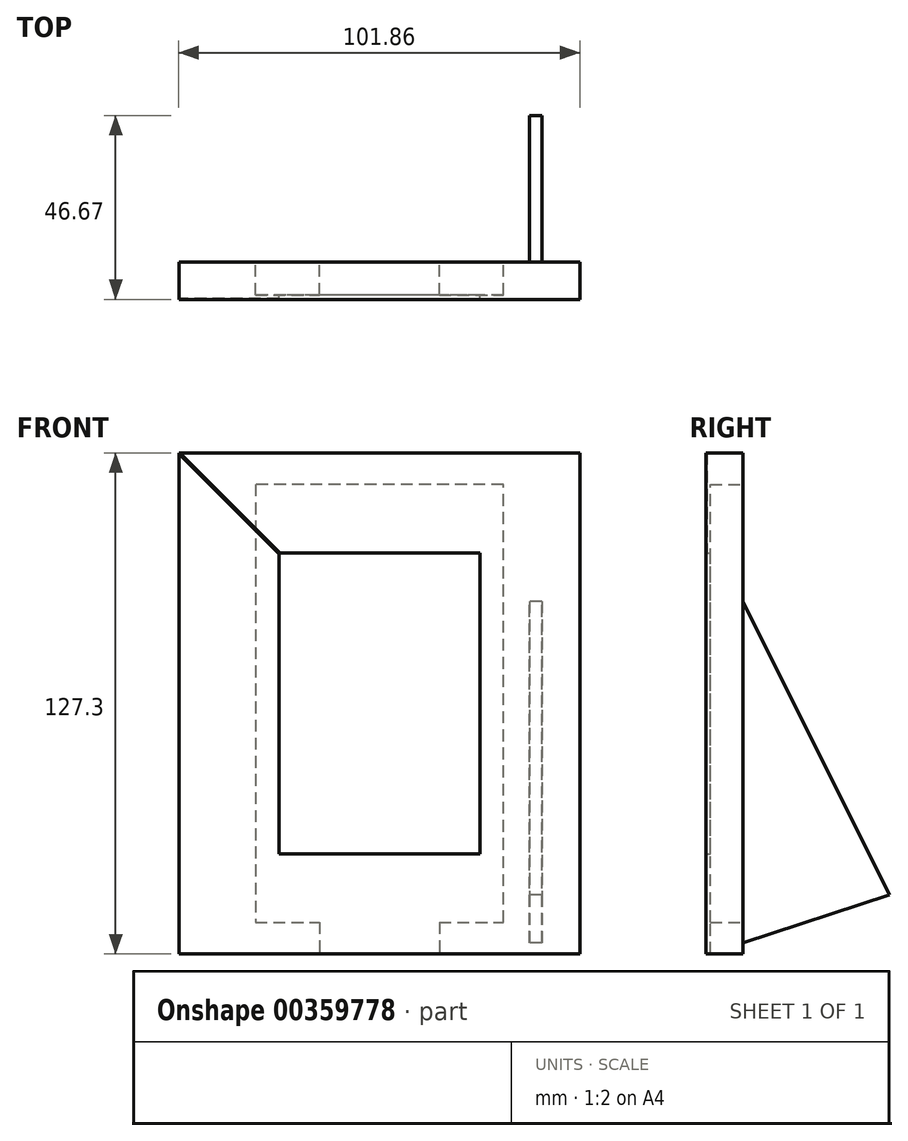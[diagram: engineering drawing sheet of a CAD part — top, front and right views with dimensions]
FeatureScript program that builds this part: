
annotation { "Feature Type Name" : "Feature", "Feature Type Description" : "" }
export const myFeature = defineFeature(function(context is Context, id is Id, definition is map)
    precondition{}
    {
        {
            var Q0;
            Q0=qCreatedBy(makeId("Front.planeOp"),FACE);
            var sketch = newSketch(context, id + "F0", { "sketchPlane" : qUnion([Q0])});
            skLineSegment(sketch, "E0.bottom", {"start": v(-22.23, 55.25) * mm, "end": v(22.23, 55.25) * mm});
            skLineSegment(sketch, "E0.top", {"start": v(-22.23, -55.25) * mm, "end": v(22.23, -55.25) * mm});
            skLineSegment(sketch, "E0.left", {"start": v(-31.12, 46.35) * mm, "end": v(-31.12, -46.36) * mm});
            skLineSegment(sketch, "E0.right", {"start": v(31.12, 46.35) * mm, "end": v(31.12, -46.36) * mm});
            skPoint(sketch, "E1.visualSharp", {"position": v(-31.12, 55.25) * mm});
            skArc(sketch, "E1.filletArc", {"start": v(-22.23, 55.24) * mm, "mid": v(-28.51, 52.64) * mm, "end": v(-31.12, 46.35) * mm});
            skPoint(sketch, "E2.visualSharp", {"position": v(-31.12, -55.25) * mm});
            skArc(sketch, "E2.filletArc", {"start": v(-31.12, -46.36) * mm, "mid": v(-28.51, -52.64) * mm, "end": v(-22.23, -55.25) * mm});
            skPoint(sketch, "E3.visualSharp", {"position": v(31.12, -55.25) * mm});
            skArc(sketch, "E3.filletArc", {"start": v(22.23, -55.25) * mm, "mid": v(28.51, -52.64) * mm, "end": v(31.12, -46.36) * mm});
            skPoint(sketch, "E4.visualSharp", {"position": v(31.12, 55.25) * mm});
            skArc(sketch, "E4.filletArc", {"start": v(31.12, 46.35) * mm, "mid": v(28.51, 52.64) * mm, "end": v(22.23, 55.25) * mm});
            skSolve(sketch);
        }
        {
            var Q0;
            Q0=makeQuery(id+"F0.imprint","IMPRINT",FACE,{"disambiguationData":[TD([[makeQuery(id+"F0.imprint","IMPRINT",EDGE,{"derivedFrom":sQuery(id+"F0.wireOp",EDGE,"E0.bottom")}),-1.0]])]});
            var sketch = newSketch(context, id + "F1", { "sketchPlane" : qUnion([Q0])});
            skLineSegment(sketch, "E5.bottom", {"start": v(-25.53, 38.25) * mm, "end": v(25.53, 38.25) * mm});
            skLineSegment(sketch, "E5.top", {"start": v(-25.53, -38.25) * mm, "end": v(25.53, -38.25) * mm});
            skLineSegment(sketch, "E5.left", {"start": v(-25.53, 38.25) * mm, "end": v(-25.53, -38.25) * mm});
            skLineSegment(sketch, "E5.right", {"start": v(25.53, 38.25) * mm, "end": v(25.53, -38.25) * mm});
            skSolve(sketch);
        }
        {
            var Q0;
            Q0=qCreatedBy(makeId("Front.planeOp"),FACE);
            var sketch = newSketch(context, id + "F2", { "sketchPlane" : qUnion([Q0])});
            skLineSegment(sketch, "E6.bottom", {"start": v(-25.53, 38.25) * mm, "end": v(25.53, 38.25) * mm});
            skLineSegment(sketch, "E6.top", {"start": v(-25.53, -38.25) * mm, "end": v(25.53, -38.25) * mm});
            skLineSegment(sketch, "E6.left", {"start": v(-25.53, 38.25) * mm, "end": v(-25.53, -38.25) * mm});
            skLineSegment(sketch, "E6.right", {"start": v(25.53, 38.25) * mm, "end": v(25.53, -38.25) * mm});
            skLineSegment(sketch, "E7.bottom", {"start": v(-50.93, 63.65) * mm, "end": v(50.93, 63.65) * mm});
            skLineSegment(sketch, "E7.top", {"start": v(-50.93, -63.65) * mm, "end": v(50.93, -63.65) * mm});
            skLineSegment(sketch, "E7.left", {"start": v(-50.93, 63.65) * mm, "end": v(-50.93, -63.65) * mm});
            skLineSegment(sketch, "E7.right", {"start": v(50.93, 63.65) * mm, "end": v(50.93, -63.65) * mm});
            skSolve(sketch);
        }
        {
            var Q0;
            Q0 = qSketchRegion(id + "F2", true);
            extrude(context, id + "F3", {"entities" : qUnion([Q0]), "depth" : 9.52 * mm});
        }
        {
            var Q0;
            Q0=makeQuery(id+"F3.opExtrude","CAP_FACE",FACE,{"disambiguationData":[OSD([sQuery(id+"F2.wireOp",EDGE,"E6.bottom"),sQuery(id+"F2.wireOp",EDGE,"E6.top"),sQuery(id+"F2.wireOp",EDGE,"E6.left"),sQuery(id+"F2.wireOp",EDGE,"E6.right"),sQuery(id+"F2.wireOp",EDGE,"E7.bottom"),sQuery(id+"F2.wireOp",EDGE,"E7.top"),sQuery(id+"F2.wireOp",EDGE,"E7.left"),sQuery(id+"F2.wireOp",EDGE,"E7.right")])],"isStart":true});
            var sketch = newSketch(context, id + "F4", { "sketchPlane" : qUnion([Q0])});
            skLineSegment(sketch, "E8", {"start": v(-31.5, 55.63) * mm, "end": v(31.5, 55.63) * mm});
            skLineSegment(sketch, "E9", {"start": v(31.5, 55.63) * mm, "end": v(31.5, -55.63) * mm});
            skLineSegment(sketch, "E10", {"start": v(31.5, -55.63) * mm, "end": v(-31.5, -55.63) * mm});
            skLineSegment(sketch, "E11", {"start": v(-31.5, -55.63) * mm, "end": v(-31.5, 55.63) * mm});
            skSolve(sketch);
        }
        {
            var Q0;
            Q0 = qSketchRegion(id + "F4", true);
            extrude(context, id + "F5", {"entities" : qUnion([Q0]), "operationType" : NewBodyOperationType.REMOVE, "oppositeDirection" : true, "depth" : 8.38 * mm});
        }
        {
            var Q0;
            Q0=qCreatedBy(makeId("Right.planeOp"),FACE);
            cPlane(context, id + "F6", {"entities" : qUnion([Q0]), "cplaneType" : CPlaneType.OFFSET, "offset" : 38.1 * mm, "width" : 152.4 * mm, "height" : 152.4 * mm});
        }
        {
            var Q0;
            Q0=qCreatedBy(id+"F6.planeOp",FACE);
            var sketch = newSketch(context, id + "F7", { "sketchPlane" : qUnion([Q0])});
            skLineSegment(sketch, "E12", {"start": v(0, 25.9) * mm, "end": v(37.14, -48.71) * mm});
            skLineSegment(sketch, "E13", {"start": v(37.14, -48.71) * mm, "end": v(0, -60.85) * mm});
            skLineSegment(sketch, "E14", {"start": v(0, -60.85) * mm, "end": v(0, 25.9) * mm});
            skSolve(sketch);
        }
        {
            var Q0;
            Q0 = qSketchRegion(id + "F7", true);
            extrude(context, id + "F8", {"entities" : qUnion([Q0]), "operationType" : NewBodyOperationType.ADD, "depth" : 3.17 * mm});
        }
        {
            var Q0;
            Q0=makeQuery(id+"F3.opExtrude","CAP_FACE",FACE,{"disambiguationData":[OSD([sQuery(id+"F2.wireOp",EDGE,"E6.bottom"),sQuery(id+"F2.wireOp",EDGE,"E6.top"),sQuery(id+"F2.wireOp",EDGE,"E6.left"),sQuery(id+"F2.wireOp",EDGE,"E6.right"),sQuery(id+"F2.wireOp",EDGE,"E7.bottom"),sQuery(id+"F2.wireOp",EDGE,"E7.top"),sQuery(id+"F2.wireOp",EDGE,"E7.left"),sQuery(id+"F2.wireOp",EDGE,"E7.right")])],"isStart":true});
            var sketch = newSketch(context, id + "F9", { "sketchPlane" : qUnion([Q0])});
            skLineSegment(sketch, "E15.bottom", {"start": v(-15.24, -55.63) * mm, "end": v(15.24, -55.63) * mm});
            skLineSegment(sketch, "E15.top", {"start": v(-15.24, -63.65) * mm, "end": v(15.24, -63.65) * mm});
            skLineSegment(sketch, "E15.left", {"start": v(-15.24, -55.63) * mm, "end": v(-15.24, -63.65) * mm});
            skLineSegment(sketch, "E15.right", {"start": v(15.24, -55.63) * mm, "end": v(15.24, -63.65) * mm});
            skSolve(sketch);
        }
        {
            var Q0;
            Q0 = qSketchRegion(id + "F9", true);
            var Q1;
            Q1=makeQuery(id+"F5.boolean.opBoolean","COPY",FACE,{"derivedFrom":makeQuery(id+"F5.opExtrude","CAP_FACE",FACE,{"disambiguationData":[OSD([sQuery(id+"F4.wireOp",EDGE,"E8"),sQuery(id+"F4.wireOp",EDGE,"E9"),sQuery(id+"F4.wireOp",EDGE,"E10"),sQuery(id+"F4.wireOp",EDGE,"E11")])],"isStart":false})});
            extrude(context, id + "F10", {"entities" : qUnion([Q0]), "operationType" : NewBodyOperationType.REMOVE, "endBound" : BoundingType.UP_TO_SURFACE, "oppositeDirection" : true, "endBoundEntityFace" : qUnion([Q1]), "depth" : 25.4 * mm});
        }
        {
            var Q0;
            Q0=makeQuery(id+"F3.opExtrude","CAP_FACE",FACE,{"disambiguationData":[OSD([sQuery(id+"F2.wireOp",EDGE,"E6.bottom"),sQuery(id+"F2.wireOp",EDGE,"E6.top"),sQuery(id+"F2.wireOp",EDGE,"E6.left"),sQuery(id+"F2.wireOp",EDGE,"E6.right"),sQuery(id+"F2.wireOp",EDGE,"E7.bottom"),sQuery(id+"F2.wireOp",EDGE,"E7.top"),sQuery(id+"F2.wireOp",EDGE,"E7.left"),sQuery(id+"F2.wireOp",EDGE,"E7.right")])],"isStart":false});
            var sketch = newSketch(context, id + "F11", { "sketchPlane" : qUnion([Q0])});
            skLineSegment(sketch, "E16", {"start": v(-25.53, 38) * mm, "end": v(-50.93, 63.4) * mm});
            skLineSegment(sketch, "E17", {"start": v(-50.93, 63.4) * mm, "end": v(-50.93, 63.65) * mm});
            skLineSegment(sketch, "E18", {"start": v(-50.93, 63.65) * mm, "end": v(-50.67, 63.65) * mm});
            skLineSegment(sketch, "E19", {"start": v(-50.67, 63.65) * mm, "end": v(-25.27, 38.25) * mm});
            skLineSegment(sketch, "E20", {"start": v(-25.27, 38.25) * mm, "end": v(-25.53, 38.25) * mm});
            skLineSegment(sketch, "E21", {"start": v(-25.53, 38.25) * mm, "end": v(-25.53, 38) * mm});
            skSolve(sketch);
        }
        {
            var Q0;
            Q0 = qSketchRegion(id + "F11", true);
            extrude(context, id + "F12", {"entities" : qUnion([Q0]), "operationType" : NewBodyOperationType.REMOVE, "oppositeDirection" : true, "depth" : 0.25 * mm});
        }
    });
